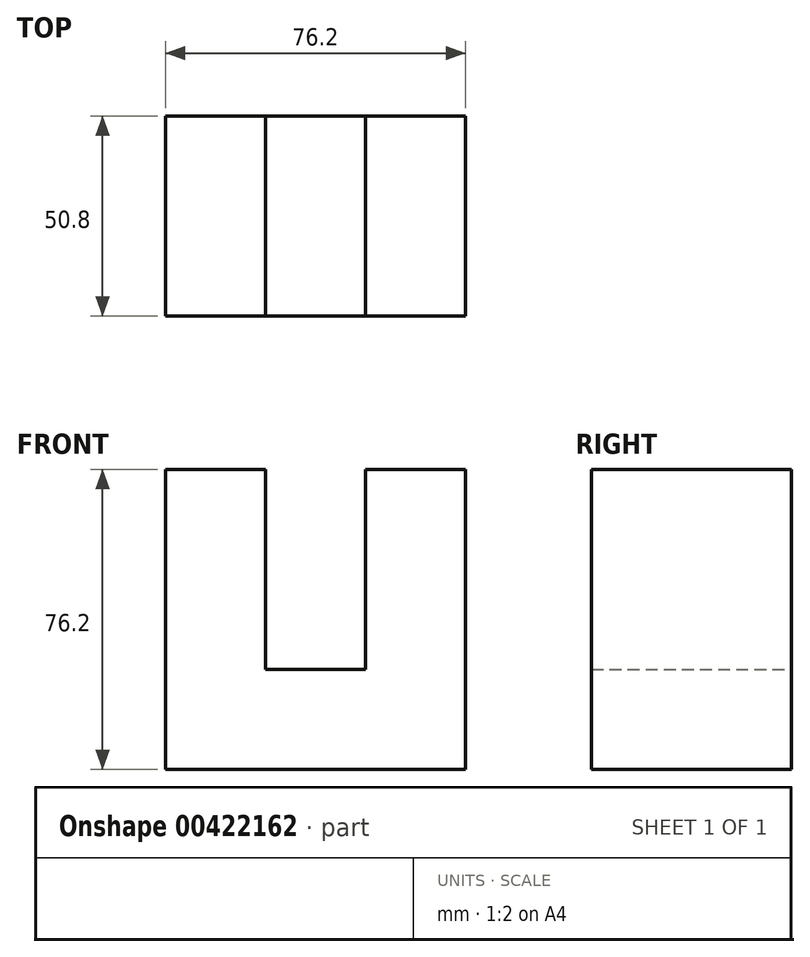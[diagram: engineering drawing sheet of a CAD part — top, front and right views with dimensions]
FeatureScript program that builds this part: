
annotation { "Feature Type Name" : "Feature", "Feature Type Description" : "" }
export const myFeature = defineFeature(function(context is Context, id is Id, definition is map)
    precondition{}
    {
        {
            var Q0;
            Q0=qCreatedBy(makeId("Front.planeOp"),FACE);
            var sketch = newSketch(context, id + "F0", { "sketchPlane" : qUnion([Q0])});
            skLineSegment(sketch, "E0", {"start": v(-27.48, -8.44) * mm, "end": v(-27.48, 42.36) * mm});
            skLineSegment(sketch, "E1", {"start": v(-27.48, 42.36) * mm, "end": v(-52.88, 42.36) * mm});
            skLineSegment(sketch, "E2", {"start": v(-52.88, 42.36) * mm, "end": v(-52.88, -33.84) * mm});
            skLineSegment(sketch, "E3", {"start": v(-52.88, -33.84) * mm, "end": v(23.32, -33.84) * mm});
            skLineSegment(sketch, "E4", {"start": v(23.32, -33.84) * mm, "end": v(23.32, 42.36) * mm});
            skLineSegment(sketch, "E5", {"start": v(23.32, 42.36) * mm, "end": v(-2.08, 42.36) * mm});
            skLineSegment(sketch, "E6", {"start": v(-2.08, 42.36) * mm, "end": v(-2.08, -8.44) * mm});
            skLineSegment(sketch, "E7", {"start": v(-27.48, -8.44) * mm, "end": v(-2.08, -8.44) * mm});
            skSolve(sketch);
        }
        {
            var Q0;
            Q0 = qSketchRegion(id + "F0", true);
            extrude(context, id + "F1", {"entities" : qUnion([Q0]), "depth" : 50.8 * mm});
        }
    });
